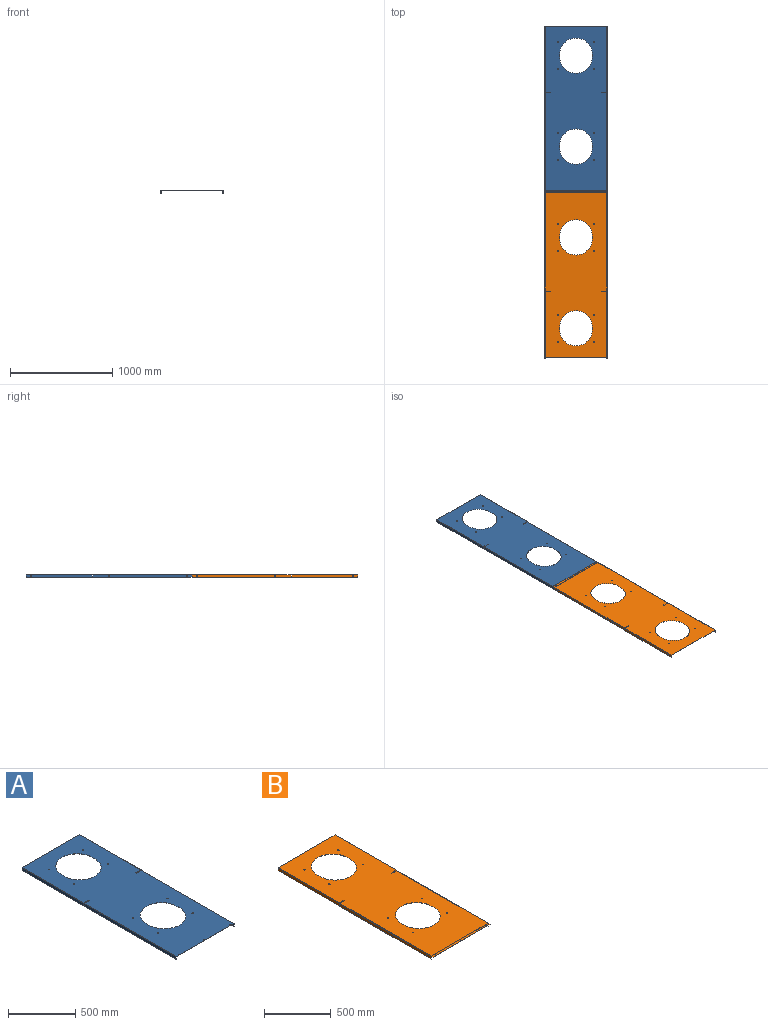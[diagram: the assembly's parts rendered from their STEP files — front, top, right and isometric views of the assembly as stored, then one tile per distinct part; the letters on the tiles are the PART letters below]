
ASSEMBLY  parts=2 mates=1
PART A: 71 faces, bbox 607x1625x26 mm
  f0: plane 647.5x1mm, normal (0,0,-1), area 647.5mm2, adj f1,f3,f4,f5
  f1: plane 24x1mm, normal (0,1,0), area 24mm2, adj f0,f4,f5,f68
  f2: cylinder r=2.5mm len=5mm, axis (1,0,0), area 15.7mm2, adj f4,f5
  f3: plane 24x1mm, normal (0,-1,0), area 24mm2, adj f0,f4,f5,f67
  f4: plane 647.5x24mm, normal (1,0,0), area 15520.4mm2, adj f0,f1,f2,f3,f70
  f5: plane 647.5x24mm, normal (-1,0,0), area 15520.4mm2, adj f0,f1,f2,f3,f69
  f6: plane 24x1mm, normal (0,-1,0), area 24mm2, adj f7,f11,f12,f63
  f7: plane 969.5x1mm, normal (0,0,-1), area 969.5mm2, adj f6,f10,f11,f12
  f8: cylinder r=2.5mm len=5mm, axis (1,0,0), area 15.7mm2, adj f11,f12
  f9: cylinder r=2.5mm len=5mm, axis (1,0,0), area 15.7mm2, adj f11,f12
  f10: plane 24x1mm, normal (0,1,0), area 24mm2, adj f7,f11,f12,f64
  f11: plane 969.5x24mm, normal (1,0,0), area 23228.7mm2, adj f6,f7,f8,f9,f10,f66
  f12: plane 969.5x24mm, normal (-1,0,0), area 23228.7mm2, adj f6,f7,f8,f9,f10,f65
  f13: plane 8x1mm, normal (1,0,0), area 8mm2, adj f14,f39,f40,f41
  f14: plane 53x1mm, normal (0,1,0), area 53mm2, adj f13,f40,f41,f60
  f15: plane 603x1mm, normal (0,-1,0), area 603mm2, adj f40,f41,f59,f63
  f16: plane 53x1mm, normal (0,1,0), area 53mm2, adj f17,f40,f41,f64
  f17: plane 8x1mm, normal (-1,0,0), area 8mm2, adj f16,f18,f40,f41
  f18: plane 53x1mm, normal (0,-1,0), area 53mm2, adj f17,f40,f41,f67
  f19: plane 603x1mm, normal (0,1,0), area 603mm2, adj f40,f41,f49,f68
  f20: plane 25x1mm, normal (-1,0,0), area 25mm2, adj f21,f38,f40,f41
  f21: cylinder r=160mm len=320mm, axis (0,0,-1), area 502.7mm2, adj f20,f22,f40,f41
  f22: plane 25x1mm, normal (1,0,0), area 25mm2, adj f21,f38,f40,f41
  f23: plane 25x1mm, normal (-1,0,0), area 25mm2, adj f24,f29,f40,f41
  f24: cylinder r=160mm len=320mm, axis (0,0,-1), area 502.7mm2, adj f23,f25,f40,f41
  f25: plane 25x1mm, normal (1,0,0), area 25mm2, adj f24,f29,f40,f41
  f26: cylinder r=2.5mm len=5mm, axis (0,0,-1), area 15.7mm2, adj f40,f41
  f27: cylinder r=2.5mm len=5mm, axis (0,0,-1), area 15.7mm2, adj f40,f41
  f28: cylinder r=2.5mm len=5mm, axis (0,0,-1), area 15.7mm2, adj f40,f41
  f29: cylinder r=160mm len=320mm, axis (0,0,-1), area 502.7mm2, adj f23,f25,f40,f41
  f30: cylinder r=4.5mm len=9mm, axis (0,0,-1), area 28.3mm2, adj f40,f41
  f31: cylinder r=4.5mm len=9mm, axis (0,0,-1), area 28.3mm2, adj f40,f41
  f32: cylinder r=4.5mm len=9mm, axis (0,0,-1), area 28.3mm2, adj f40,f41
  f33: cylinder r=4.5mm len=9mm, axis (0,0,-1), area 28.3mm2, adj f40,f41
  f34: cylinder r=4.5mm len=9mm, axis (0,0,-1), area 28.3mm2, adj f40,f41
  f35: cylinder r=4.5mm len=9mm, axis (0,0,-1), area 28.3mm2, adj f40,f41
  f36: cylinder r=4.5mm len=9mm, axis (0,0,-1), area 28.3mm2, adj f40,f41
  f37: cylinder r=4.5mm len=9mm, axis (0,0,-1), area 28.3mm2, adj f40,f41
  f38: cylinder r=160mm len=320mm, axis (0,0,-1), area 502.7mm2, adj f20,f22,f40,f41
  f39: plane 53x1mm, normal (0,-1,0), area 53mm2, adj f13,f40,f41,f48
  f40: plane 1625x603mm, normal (0,0,-1), area 801609.6mm2, adj f13,f14,f15,f16,f17,f18,f19,f20
  f41: plane 1625x603mm, normal (0,0,1), area 801609.6mm2, adj f13,f14,f15,f16,f17,f18,f19,f20
  f42: plane 24x1mm, normal (0,1,0), area 24mm2, adj f43,f46,f47,f49
  f43: plane 647.5x1mm, normal (0,0,-1), area 647.5mm2, adj f42,f45,f46,f47
  f44: cylinder r=2.5mm len=5mm, axis (-1,0,0), area 15.7mm2, adj f46,f47
  f45: plane 24x1mm, normal (0,-1,0), area 24mm2, adj f43,f46,f47,f48
  f46: plane 647.5x24mm, normal (-1,0,0), area 15520.4mm2, adj f42,f43,f44,f45,f51
  f47: plane 647.5x24mm, normal (1,0,0), area 15520.4mm2, adj f42,f43,f44,f45,f50
  f48: plane 2x2mm, normal (0,-1,0), area 2.4mm2, adj f39,f45,f50,f51
  f49: plane 2x2mm, normal (0,1,0), area 2.4mm2, adj f19,f42,f50,f51
  f50: cylinder r=2mm len=647.5mm, axis (0,-1,0), area 2034.2mm2, adj f41,f47,f48,f49
  f51: cylinder r=1mm len=647.5mm, axis (0,-1,0), area 1017.1mm2, adj f40,f46,f48,f49
  f52: plane 969.5x1mm, normal (0,0,-1), area 969.5mm2, adj f53,f56,f57,f58
  f53: plane 24x1mm, normal (0,-1,0), area 24mm2, adj f52,f57,f58,f59
  f54: cylinder r=2.5mm len=5mm, axis (-1,0,0), area 15.7mm2, adj f57,f58
  f55: cylinder r=2.5mm len=5mm, axis (-1,0,0), area 15.7mm2, adj f57,f58
  f56: plane 24x1mm, normal (0,1,0), area 24mm2, adj f52,f57,f58,f60
  f57: plane 969.5x24mm, normal (-1,0,0), area 23228.7mm2, adj f52,f53,f54,f55,f56,f62
  f58: plane 969.5x24mm, normal (1,0,0), area 23228.7mm2, adj f52,f53,f54,f55,f56,f61
  f59: plane 2x2mm, normal (0,-1,0), area 2.4mm2, adj f15,f53,f61,f62
  f60: plane 2x2mm, normal (0,1,0), area 2.4mm2, adj f14,f56,f61,f62
  f61: cylinder r=2mm len=969.5mm, axis (0,-1,0), area 3045.8mm2, adj f41,f58,f59,f60
  f62: cylinder r=1mm len=969.5mm, axis (0,-1,0), area 1522.9mm2, adj f40,f57,f59,f60
  f63: plane 2x2mm, normal (0,-1,0), area 2.4mm2, adj f6,f15,f65,f66
  f64: plane 2x2mm, normal (0,1,0), area 2.4mm2, adj f10,f16,f65,f66
  f65: cylinder r=2mm len=969.5mm, axis (0,-1,0), area 3045.8mm2, adj f12,f41,f63,f64
  f66: cylinder r=1mm len=969.5mm, axis (0,-1,0), area 1522.9mm2, adj f11,f40,f63,f64
  f67: plane 2x2mm, normal (0,-1,0), area 2.4mm2, adj f3,f18,f69,f70
  f68: plane 2x2mm, normal (0,1,0), area 2.4mm2, adj f1,f19,f69,f70
  f69: cylinder r=2mm len=647.5mm, axis (0,-1,0), area 2034.2mm2, adj f5,f41,f67,f68
  f70: cylinder r=1mm len=647.5mm, axis (0,-1,0), area 1017.1mm2, adj f4,f40,f67,f68
PART B: 89 faces, bbox 607x1644.4x27.2 mm
  f0: plane 8x1mm, normal (1,0,0), area 8mm2, adj f1,f22,f23,f24
  f1: plane 53x1mm, normal (0,1,0), area 53mm2, adj f0,f23,f24,f80
  f2: plane 53x1mm, normal (0,1,0), area 53mm2, adj f3,f23,f24,f68
  f3: plane 8x1mm, normal (-1,0,0), area 8mm2, adj f2,f4,f23,f24
  f4: plane 53x1mm, normal (0,-1,0), area 53mm2, adj f3,f23,f24,f55
  f5: plane 603x1mm, normal (0,1,0), area 603mm2, adj f23,f24,f52,f56
  f6: plane 25x1mm, normal (-1,0,0), area 25mm2, adj f7,f21,f23,f24
  f7: cylinder r=160mm len=320mm, axis (0,0,-1), area 502.7mm2, adj f6,f8,f23,f24
  f8: plane 25x1mm, normal (1,0,0), area 25mm2, adj f7,f21,f23,f24
  f9: plane 25x1mm, normal (-1,0,0), area 25mm2, adj f10,f12,f23,f24
  f10: cylinder r=160mm len=320mm, axis (0,0,-1), area 502.7mm2, adj f9,f11,f23,f24
  f11: plane 25x1mm, normal (1,0,0), area 25mm2, adj f10,f12,f23,f24
  f12: cylinder r=160mm len=320mm, axis (0,0,-1), area 502.7mm2, adj f9,f11,f23,f24
  f13: cylinder r=4.5mm len=9mm, axis (0,0,-1), area 28.3mm2, adj f23,f24
  f14: cylinder r=4.5mm len=9mm, axis (0,0,-1), area 28.3mm2, adj f23,f24
  f15: cylinder r=4.5mm len=9mm, axis (0,0,-1), area 28.3mm2, adj f23,f24
  f16: cylinder r=4.5mm len=9mm, axis (0,0,-1), area 28.3mm2, adj f23,f24
  f17: cylinder r=4.5mm len=9mm, axis (0,0,-1), area 28.3mm2, adj f23,f24
  f18: cylinder r=4.5mm len=9mm, axis (0,0,-1), area 28.3mm2, adj f23,f24
  f19: cylinder r=4.5mm len=9mm, axis (0,0,-1), area 28.3mm2, adj f23,f24
  f20: cylinder r=4.5mm len=9mm, axis (0,0,-1), area 28.3mm2, adj f23,f24
  f21: cylinder r=160mm len=320mm, axis (0,0,-1), area 502.7mm2, adj f6,f8,f23,f24
  f22: plane 53x1mm, normal (0,-1,0), area 53mm2, adj f0,f23,f24,f51
  f23: plane 1624.12x603mm, normal (0,0,-1), area 801139.8mm2, adj f0,f1,f2,f3,f4,f5,f6,f7
  f24: plane 1624.12x603mm, normal (0,0,1), area 801139.8mm2, adj f0,f1,f2,f3,f4,f5,f6,f7
  f25: plane 603x1mm, normal (0,-1,0), area 603mm2, adj f26,f30,f31,f32
  f26: plane 19.12x1mm, normal (-1,0,0), area 19.1mm2, adj f25,f31,f32,f33
  f27: cylinder r=2.5mm len=5mm, axis (0,0,-1), area 15.7mm2, adj f31,f32
  f28: cylinder r=2.5mm len=5mm, axis (0,0,-1), area 15.7mm2, adj f31,f32
  f29: cylinder r=2.5mm len=5mm, axis (0,0,-1), area 15.7mm2, adj f31,f32
  f30: plane 19.12x1mm, normal (1,0,0), area 19.1mm2, adj f25,f31,f32,f34
  f31: plane 603x19.12mm, normal (0,0,-1), area 11472.3mm2, adj f25,f26,f27,f28,f29,f30,f36
  f32: plane 603x19.12mm, normal (0,0,1), area 11472.3mm2, adj f25,f26,f27,f28,f29,f30,f35
  f33: plane 1.04x1.03mm, normal (-1,0,0), area 0.8mm2, adj f26,f35,f36,f37
  f34: plane 1.04x1.03mm, normal (1,0,0), area 0.8mm2, adj f30,f35,f36,f38
  f35: cylinder r=1.04mm len=603mm, axis (-1,0,0), area 879.8mm2, adj f32,f33,f34,f40
  f36: cylinder r=0.05mm len=603mm, axis (-1,0,0), area 37.9mm2, adj f31,f33,f34,f39
  f37: plane 1.05x0.51mm, normal (-1,0,0), area 0.3mm2, adj f33,f39,f40,f41
  f38: plane 1.05x0.51mm, normal (1,0,0), area 0.3mm2, adj f34,f39,f40,f42
  f39: plane 603x0.34mm, normal (0,-0.98,-0.17), area 208.8mm2, adj f36,f37,f38,f43
  f40: plane 603x0.34mm, normal (0,0.98,0.17), area 208.8mm2, adj f35,f37,f38,f44
  f41: plane 1.04x1.03mm, normal (-1,0,0), area 0.8mm2, adj f37,f43,f44,f67
  f42: plane 1.04x1.03mm, normal (1,0,0), area 0.8mm2, adj f38,f43,f44,f79
  f43: cylinder r=1.04mm len=603mm, axis (-1,0,0), area 879.8mm2, adj f23,f39,f41,f42
  f44: cylinder r=0.05mm len=603mm, axis (-1,0,0), area 37.9mm2, adj f24,f40,f41,f42
  f45: plane 24x1mm, normal (0,1,0), area 24mm2, adj f46,f49,f50,f52
  f46: plane 647.5x1mm, normal (0,0,-1), area 647.5mm2, adj f45,f48,f49,f50
  f47: cylinder r=2.5mm len=5mm, axis (-1,0,0), area 15.7mm2, adj f49,f50
  f48: plane 24x1mm, normal (0,-1,0), area 24mm2, adj f46,f49,f50,f51
  f49: plane 647.5x24mm, normal (-1,0,0), area 15520.4mm2, adj f45,f46,f47,f48,f54
  f50: plane 647.5x24mm, normal (1,0,0), area 15520.4mm2, adj f45,f46,f47,f48,f53
  f51: plane 2x2mm, normal (0,-1,0), area 2.4mm2, adj f22,f48,f53,f54
  f52: plane 2x2mm, normal (0,1,0), area 2.4mm2, adj f5,f45,f53,f54
  f53: cylinder r=2mm len=647.5mm, axis (0,-1,0), area 2034.2mm2, adj f24,f50,f51,f52
  f54: cylinder r=1mm len=647.5mm, axis (0,-1,0), area 1017.1mm2, adj f23,f49,f51,f52
  f55: plane 2x2mm, normal (0,-1,0), area 2.4mm2, adj f4,f57,f58,f86
  f56: plane 2x2mm, normal (0,1,0), area 2.4mm2, adj f5,f57,f58,f84
  f57: cylinder r=2mm len=647.5mm, axis (0,-1,0), area 2034.2mm2, adj f24,f55,f56,f88
  f58: cylinder r=1mm len=647.5mm, axis (0,-1,0), area 1017.1mm2, adj f23,f55,f56,f87
  f59: plane 1x0.88mm, normal (0,0,1), area 0.9mm2, adj f60,f65,f66,f67
  f60: plane 24x1mm, normal (0,-1,0), area 24mm2, adj f59,f61,f65,f66
  f61: plane 969.5x1mm, normal (0,0,-1), area 969.5mm2, adj f60,f64,f65,f66
  f62: cylinder r=2.5mm len=5mm, axis (1,0,0), area 15.7mm2, adj f65,f66
  f63: cylinder r=2.5mm len=5mm, axis (1,0,0), area 15.7mm2, adj f65,f66
  f64: plane 24x1mm, normal (0,1,0), area 24mm2, adj f61,f65,f66,f68
  f65: plane 969.5x24mm, normal (1,0,0), area 23228.7mm2, adj f59,f60,f61,f62,f63,f64,f70
  f66: plane 969.5x24mm, normal (-1,0,0), area 23228.7mm2, adj f59,f60,f61,f62,f63,f64,f69
  f67: plane 2x2mm, normal (0,-1,0), area 2.4mm2, adj f41,f59,f69,f70
  f68: plane 2x2mm, normal (0,1,0), area 2.4mm2, adj f2,f64,f69,f70
  f69: cylinder r=2mm len=968.62mm, axis (0,-1,0), area 3043mm2, adj f24,f66,f67,f68
  f70: cylinder r=1mm len=968.62mm, axis (0,-1,0), area 1521.5mm2, adj f23,f65,f67,f68
  f71: plane 969.5x1mm, normal (0,0,-1), area 969.5mm2, adj f72,f76,f77,f78
  f72: plane 24x1mm, normal (0,-1,0), area 24mm2, adj f71,f73,f77,f78
  f73: plane 1x0.88mm, normal (0,0,1), area 0.9mm2, adj f72,f77,f78,f79
  f74: cylinder r=2.5mm len=5mm, axis (-1,0,0), area 15.7mm2, adj f77,f78
  f75: cylinder r=2.5mm len=5mm, axis (-1,0,0), area 15.7mm2, adj f77,f78
  f76: plane 24x1mm, normal (0,1,0), area 24mm2, adj f71,f77,f78,f80
  f77: plane 969.5x24mm, normal (-1,0,0), area 23228.7mm2, adj f71,f72,f73,f74,f75,f76,f82
  f78: plane 969.5x24mm, normal (1,0,0), area 23228.7mm2, adj f71,f72,f73,f74,f75,f76,f81
  f79: plane 2x2mm, normal (0,-1,0), area 2.4mm2, adj f42,f73,f81,f82
  f80: plane 2x2mm, normal (0,1,0), area 2.4mm2, adj f1,f76,f81,f82
  f81: cylinder r=2mm len=968.62mm, axis (0,-1,0), area 3043mm2, adj f24,f78,f79,f80
  f82: cylinder r=1mm len=968.62mm, axis (0,-1,0), area 1521.5mm2, adj f23,f77,f79,f80
  f83: plane 647.5x1mm, normal (0,0,-1), area 647.5mm2, adj f84,f86,f87,f88
  f84: plane 24x1mm, normal (0,1,0), area 24mm2, adj f56,f83,f87,f88
  f85: cylinder r=2.5mm len=5mm, axis (1,0,0), area 15.7mm2, adj f87,f88
  f86: plane 24x1mm, normal (0,-1,0), area 24mm2, adj f55,f83,f87,f88
  f87: plane 647.5x24mm, normal (1,0,0), area 15520.4mm2, adj f58,f83,f84,f85,f86
  f88: plane 647.5x24mm, normal (-1,0,0), area 15520.4mm2, adj f57,f83,f84,f85,f86
PLACE A t=(9.51,2.98,8.74)mm fixed
PLACE B rot(axis=(0,0,-1),180deg) t=(9.51,-1622.02,8.74)mm
MATE fastened B.f78 <-> A.f12  axis (-1,0,0) through (-293.99,-809.52,-16.26)mm
